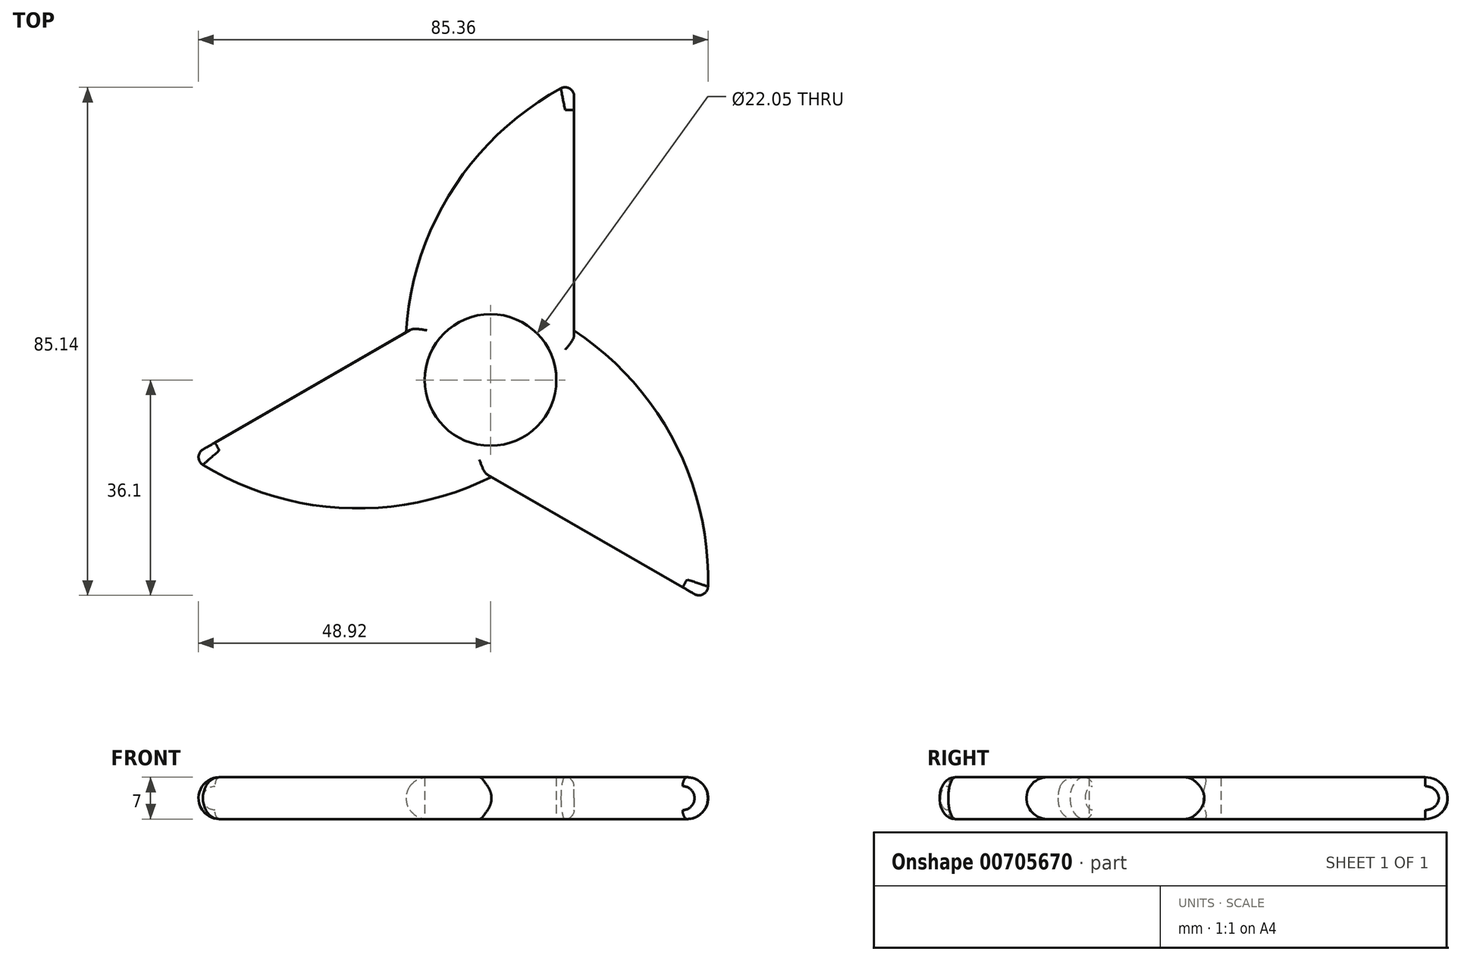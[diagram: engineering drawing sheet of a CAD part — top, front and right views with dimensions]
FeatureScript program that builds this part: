
annotation { "Feature Type Name" : "Feature", "Feature Type Description" : "" }
export const myFeature = defineFeature(function(context is Context, id is Id, definition is map)
    precondition{}
    {
        {
            var Q0;
            Q0=qCreatedBy(makeId("Top.planeOp"),FACE);
            var sketch = newSketch(context, id + "F0", { "sketchPlane" : qUnion([Q0])});
            skCircle(sketch, "E0", {"center": v(0, 0) * mm, "radius": 11.03 * mm});
            skCircle(sketch, "E1", {"center": v(0, 0) * mm, "radius": 14 * mm});
            skLineSegment(sketch, "E2", {"start": v(14, 0) * mm, "end": v(14, 50) * mm});
            skArc(sketch, "E3", {"start": v(14, 50) * mm, "mid": v(-7.87, 29.4) * mm, "end": v(-14, 0) * mm});
            skSolve(sketch);
        }
        {
            var Q0;
            {var subQ0=sQuery(id+"F0.wireOp",EDGE,"E2");Q0=makeQuery(id+"F0.imprint","IMPRINT",FACE,{"disambiguationData":[TD([[makeQuery(id+"F0.imprint","IMPRINT",EDGE,{"derivedFrom":subQ0}),1.0]])]});}
            var Q1;
            Q1=makeQuery(id+"F0.imprint","IMPRINT",FACE,{"disambiguationData":[TD([[makeQuery(id+"F0.imprint","IMPRINT",EDGE,{"derivedFrom":sQuery(id+"F0.wireOp",EDGE,"E0")}),-1.0]])]});
            extrude(context, id + "F1", {"entities" : qUnion([Q0, Q1]), "depth" : 7 * mm, "offsetDistance" : 25 * mm});
        }
        {
            var Q0;
            Q0=makeQuery(id+"F1.opExtrude","SWEPT_BODY",BODY,{"disambiguationData":[OSD([sQuery(id+"F0.wireOp",EDGE,"E0"),sQuery(id+"F0.wireOp",EDGE,"E1"),sQuery(id+"F0.wireOp",EDGE,"E2"),sQuery(id+"F0.wireOp",EDGE,"E3")])]});
            var Q1;
            Q1=makeQuery(id+"F1.opExtrude","CAP_EDGE",EDGE,{"disambiguationData":[OSD([sQuery(id+"F0.wireOp",EDGE,"E0")])],"isStart":false});
            circularPattern(context, id + "F2", {"operationType" : NewBodyOperationType.ADD, "entities" : qUnion([Q0]), "axis" : qUnion([Q1]), "angle" : 360 * degree, "instanceCount" : 3, "equalSpace" : true});
        }
        {
            var Q0;
            Q0=makeQuery(id+"F2.opPattern","COPY",EDGE,{"derivedFrom":makeQuery(id+"F1.opExtrude","CAP_EDGE",EDGE,{"disambiguationData":[OSD([sQuery(id+"F0.wireOp",EDGE,"E3")])],"isStart":false}),"instanceName":"2"});
            var Q1;
            Q1=makeQuery(id+"F2.opPattern","COPY",EDGE,{"derivedFrom":makeQuery(id+"F1.opExtrude","CAP_EDGE",EDGE,{"disambiguationData":[OSD([sQuery(id+"F0.wireOp",EDGE,"E3")])],"isStart":true}),"instanceName":"2"});
            var Q2;
            Q2=makeQuery(id+"F2.opPattern","COPY",EDGE,{"derivedFrom":makeQuery(id+"F1.opExtrude","CAP_EDGE",EDGE,{"disambiguationData":[OSD([sQuery(id+"F0.wireOp",EDGE,"E3")])],"isStart":false}),"instanceName":"1"});
            var Q3;
            Q3=makeQuery(id+"F2.opPattern","COPY",EDGE,{"derivedFrom":makeQuery(id+"F1.opExtrude","CAP_EDGE",EDGE,{"disambiguationData":[OSD([sQuery(id+"F0.wireOp",EDGE,"E3")])],"isStart":true}),"instanceName":"1"});
            var Q4;
            Q4=makeQuery(id+"F1.opExtrude","CAP_EDGE",EDGE,{"disambiguationData":[OSD([sQuery(id+"F0.wireOp",EDGE,"E3")])],"isStart":false});
            var Q5;
            Q5=makeQuery(id+"F1.opExtrude","CAP_EDGE",EDGE,{"disambiguationData":[OSD([sQuery(id+"F0.wireOp",EDGE,"E3")])],"isStart":true});
            fillet(context, id + "F3", {"entities" : qUnion([Q0, Q1, Q2, Q3, Q4, Q5]), "radius" : 3.5 * mm, "tangentPropagation" : true, "allowEdgeOverflow" : false});
        }
        {
            var Q0;
            Q0=makeQuery(id+"F2.opPattern","COPY",EDGE,{"derivedFrom":makeQuery(id+"F1.opExtrude","CAP_EDGE",EDGE,{"disambiguationData":[OSD([sQuery(id+"F0.wireOp",EDGE,"E2")])],"isStart":false}),"instanceName":"2"});
            var Q1;
            Q1=makeQuery(id+"F2.opPattern","COPY",EDGE,{"derivedFrom":makeQuery(id+"F1.opExtrude","CAP_EDGE",EDGE,{"disambiguationData":[OSD([sQuery(id+"F0.wireOp",EDGE,"E2")])],"isStart":true}),"instanceName":"2"});
            var Q2;
            Q2=makeQuery(id+"F1.opExtrude","CAP_EDGE",EDGE,{"disambiguationData":[OSD([sQuery(id+"F0.wireOp",EDGE,"E2")])],"isStart":true});
            var Q3;
            Q3=makeQuery(id+"F1.opExtrude","CAP_EDGE",EDGE,{"disambiguationData":[OSD([sQuery(id+"F0.wireOp",EDGE,"E2")])],"isStart":false});
            var Q4;
            Q4=makeQuery(id+"F2.opPattern","COPY",EDGE,{"derivedFrom":makeQuery(id+"F1.opExtrude","CAP_EDGE",EDGE,{"disambiguationData":[OSD([sQuery(id+"F0.wireOp",EDGE,"E2")])],"isStart":false}),"instanceName":"1"});
            var Q5;
            Q5=makeQuery(id+"F2.opPattern","COPY",EDGE,{"derivedFrom":makeQuery(id+"F1.opExtrude","CAP_EDGE",EDGE,{"disambiguationData":[OSD([sQuery(id+"F0.wireOp",EDGE,"E2")])],"isStart":true}),"instanceName":"1"});
            fillet(context, id + "F4", {"entities" : qUnion([Q0, Q1, Q2, Q3, Q4, Q5]), "radius" : 1.5 * mm, "tangentPropagation" : true, "allowEdgeOverflow" : false});
        }
    });
